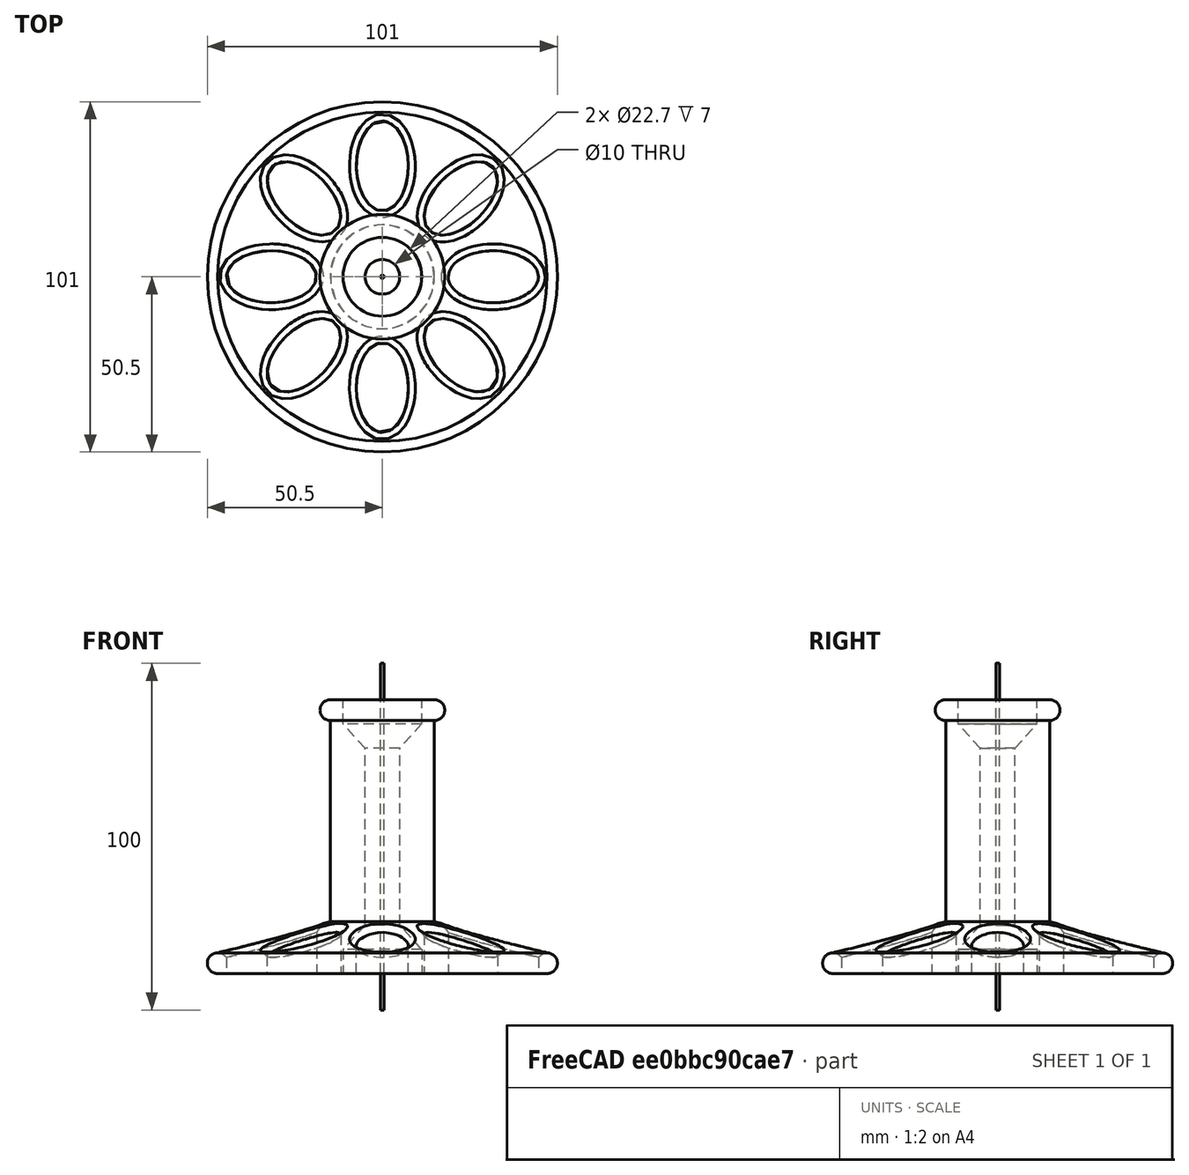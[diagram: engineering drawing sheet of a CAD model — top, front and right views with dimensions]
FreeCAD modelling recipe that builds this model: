
FCSTD DOCUMENT  (FreeCAD 0.19R24267 +99 (Git))
Label: Spool
License: All rights reserved
LicenseURL: http://en.wikipedia.org/wiki/All_rights_reserved
objects: Part::Cylinder×13, Part::Feature×8, Part::Cone×3, Part::MultiFuse×3, Part::Chamfer×3, Part::Part2DObjectPython×2, Part::FeaturePython×2, Part::Revolution×2, Part::Fuse×2, Part::Cut×1, Part::Refine×1
note: 40 computed .brp shape members not serialized (recipe doc carries the construction recipe); baked Part::Feature solids carry a one-line shape summary decoded from their .brp

FEATURE [Part::Cylinder] cylinder
  Angle = 360
  AttacherType = Attacher::AttachEngine3D
  Height = 79
  Placement = pos=(0,0,-39.5) rot=(0,0,1;0rad)
  Radius = 15
FEATURE [Part::Cone] cylinder001
  Angle = 360
  AttacherType = Attacher::AttachEngine3D
  Height = 9
  Placement = pos=(0,0,-33.5) rot=(0,0,1;0rad)
  Radius1 = 47.5
  Radius2 = 15
FEATURE [Part::Cylinder] cylinder002
  Angle = 360
  AttacherType = Attacher::AttachEngine3D
  Height = 6
  Placement = pos=(0,0,-39.5) rot=(0,0,1;0rad)
  Radius = 47.5
FEATURE [Part::Part2DObjectPython] circle  # Draft 2D object (typed FeaturePython)
  Area = 28.2743
  FirstAngle = 0
  LastAngle = 0
  MakeFace = true
  Placement = pos=(15,0,0) rot=(0,0,1;0rad)
  Radius = 3
FEATURE [Part::FeaturePython] RefineRotateExtrude  # WARN: FeaturePython — macro-defined, semantics opaque (R4)
  Base = -> circle
FEATURE [Part::Revolution] RotateExtrude
  Angle = 360
  Axis = (0,1,0)
  Base = (0,0,0)
  FaceMakerClass = Part::FaceMakerBullseye
  Placement = pos=(0,0,36.5) rot=(1,0,0;1.5708rad)
  Solid = false
  Source = -> RefineRotateExtrude
  Symmetric = false
FEATURE [Part::Part2DObjectPython] circle001  # Draft 2D object (typed FeaturePython)
  Area = 28.2743
  FirstAngle = 0
  LastAngle = 0
  MakeFace = true
  Placement = pos=(47.5,0,0) rot=(0,0,1;0rad)
  Radius = 3
FEATURE [Part::FeaturePython] RefineRotateExtrude001  # WARN: FeaturePython — macro-defined, semantics opaque (R4)
  Base = -> circle001
FEATURE [Part::Revolution] RotateExtrude001
  Angle = 360
  Axis = (0,1,0)
  Base = (0,0,0)
  FaceMakerClass = Part::FaceMakerBullseye
  Placement = pos=(0,0,-36.5) rot=(1,0,0;1.5708rad)
  Solid = false
  Source = -> RefineRotateExtrude001
  Symmetric = false
FEATURE [Part::MultiFuse] union
  Shapes = -> [cylinder,cylinder001,cylinder002,RotateExtrude,RotateExtrude001]
FEATURE [Part::Cylinder] cylinder003
  Angle = 360
  AttacherType = Attacher::AttachEngine3D
  Height = 14
  Placement = pos=(0,0,32.5) rot=(0,0,1;0rad)
  Radius = 11.35
FEATURE [Part::Cylinder] cylinder004
  Angle = 360
  AttacherType = Attacher::AttachEngine3D
  Height = 14
  Placement = pos=(0,-4e-15,-32.5) rot=(1,0,0;3.14159rad)
  Radius = 11.35
FEATURE [Part::Fuse] Group
  Base = -> cylinder003
  Tool = -> cylinder004
FEATURE [Part::Cone] cylinder005
  Angle = 360
  AttacherType = Attacher::AttachEngine3D
  Height = 7
  Placement = pos=(0,0,-32.51) rot=(0,0,1;0rad)
  Radius1 = 11.35
  Radius2 = 5
FEATURE [Part::Cone] cylinder006
  Angle = 360
  AttacherType = Attacher::AttachEngine3D
  Height = 7
  Placement = pos=(0,4e-15,32.51) rot=(1,0,0;3.14159rad)
  Radius1 = 11.35
  Radius2 = 5
FEATURE [Part::Fuse] Group001
  Base = -> cylinder005
  Tool = -> cylinder006
FEATURE [Part::Cylinder] cylinder007
  Angle = 360
  AttacherType = Attacher::AttachEngine3D
  Height = 100
  Placement = pos=(0,0,-50) rot=(0,0,1;0rad)
  Radius = 5
FEATURE [Part::Cylinder] cylinder008
  Angle = 360
  AttacherType = Attacher::AttachEngine3D
  Height = 100
  Placement = pos=(0,0,-50) rot=(0,0,1;0rad)
  Radius = 0.5
FEATURE [Part::Feature] Matrix_Deformation
  Placement = pos=(0,32,-50) rot=(0,0,1;0rad)
  shape: bbox 22.5 x 45.03 x 100 mm, 3 faces (baked)
FEATURE [Part::Cylinder] cylinder009
  Angle = 360
  AttacherType = Attacher::AttachEngine3D
  Height = 100
  Placement = pos=(0,0,-50) rot=(0,0,1;0rad)
  Radius = 0.5
FEATURE [Part::Feature] Matrix_Deformation001
  Placement = pos=(-22.6274,22.6274,-50) rot=(0,0,1;0.785398rad)
  shape: bbox 35.72 x 35.72 x 100 mm, 3 faces (baked)
FEATURE [Part::Cylinder] cylinder010
  Angle = 360
  AttacherType = Attacher::AttachEngine3D
  Height = 100
  Placement = pos=(0,0,-50) rot=(0,0,1;0rad)
  Radius = 0.5
FEATURE [Part::Feature] Matrix_Deformation002
  Placement = pos=(-32,0,-50) rot=(0,0,1;1.5708rad)
  shape: bbox 45.03 x 22.5 x 100 mm, 3 faces (baked)
FEATURE [Part::Cylinder] cylinder011
  Angle = 360
  AttacherType = Attacher::AttachEngine3D
  Height = 100
  Placement = pos=(0,0,-50) rot=(0,0,1;0rad)
  Radius = 0.5
FEATURE [Part::Feature] Matrix_Deformation003
  Placement = pos=(-22.6274,-22.6274,-50) rot=(0,0,1;2.35619rad)
  shape: bbox 35.72 x 35.72 x 100 mm, 3 faces (baked)
FEATURE [Part::Cylinder] cylinder012
  Angle = 360
  AttacherType = Attacher::AttachEngine3D
  Height = 100
  Placement = pos=(0,0,-50) rot=(0,0,1;0rad)
  Radius = 0.5
FEATURE [Part::Feature] Matrix_Deformation004
  Placement = pos=(-3.9e-15,-32,-50) rot=(0,0,1;3.14159rad)
  shape: bbox 22.5 x 45.03 x 100 mm, 3 faces (baked)
FEATURE [Part::Cylinder] cylinder013
  Angle = 360
  AttacherType = Attacher::AttachEngine3D
  Height = 100
  Placement = pos=(0,0,-50) rot=(0,0,1;0rad)
  Radius = 0.5
FEATURE [Part::Feature] Matrix_Deformation005
  Placement = pos=(22.6274,-22.6274,-50) rot=(0,0,1;3.92699rad)
  shape: bbox 35.72 x 35.72 x 100 mm, 3 faces (baked)
FEATURE [Part::Cylinder] cylinder014
  Angle = 360
  AttacherType = Attacher::AttachEngine3D
  Height = 100
  Placement = pos=(0,0,-50) rot=(0,0,1;0rad)
  Radius = 0.5
FEATURE [Part::Feature] Matrix_Deformation006
  Placement = pos=(32,0,-50) rot=(0,0,-1;1.5708rad)
  shape: bbox 45.03 x 22.5 x 100 mm, 3 faces (baked)
FEATURE [Part::Cylinder] cylinder015
  Angle = 360
  AttacherType = Attacher::AttachEngine3D
  Height = 100
  Placement = pos=(0,0,-50) rot=(0,0,1;0rad)
  Radius = 0.5
FEATURE [Part::Feature] Matrix_Deformation007
  Placement = pos=(22.6274,22.6274,-50) rot=(0,0,-1;0.785398rad)
  shape: bbox 35.72 x 35.72 x 100 mm, 3 faces (baked)
FEATURE [Part::MultiFuse] Group002
  Shapes = -> [Matrix_Deformation,Matrix_Deformation001,Matrix_Deformation002,Matrix_Deformation003,Matrix_Deformation004,Matrix_Deformation005,Matrix_Deformation006,Matrix_Deformation007]
FEATURE [Part::MultiFuse] union001
  Shapes = -> [Group,Group001,cylinder007,Group002]
FEATURE [Part::Cut] difference
  Base = -> union
  Tool = -> union001
FEATURE [Part::Refine] difference001
  Source = -> difference
FEATURE [Part::Chamfer] Chamfer
  Base = -> difference001
  Edges = 1 edges r=2: [Edge12]
FEATURE [Part::Chamfer] Chamfer001
  Base = -> Chamfer
  Edges = 6 edges r=2: [Edge8,Edge9,Edge11,Edge12,Edge13,Edge14]
FEATURE [Part::Chamfer] Chamfer002  label="Final"
  Base = -> Chamfer001
  Edges = 1 edges r=2: [Edge9]
